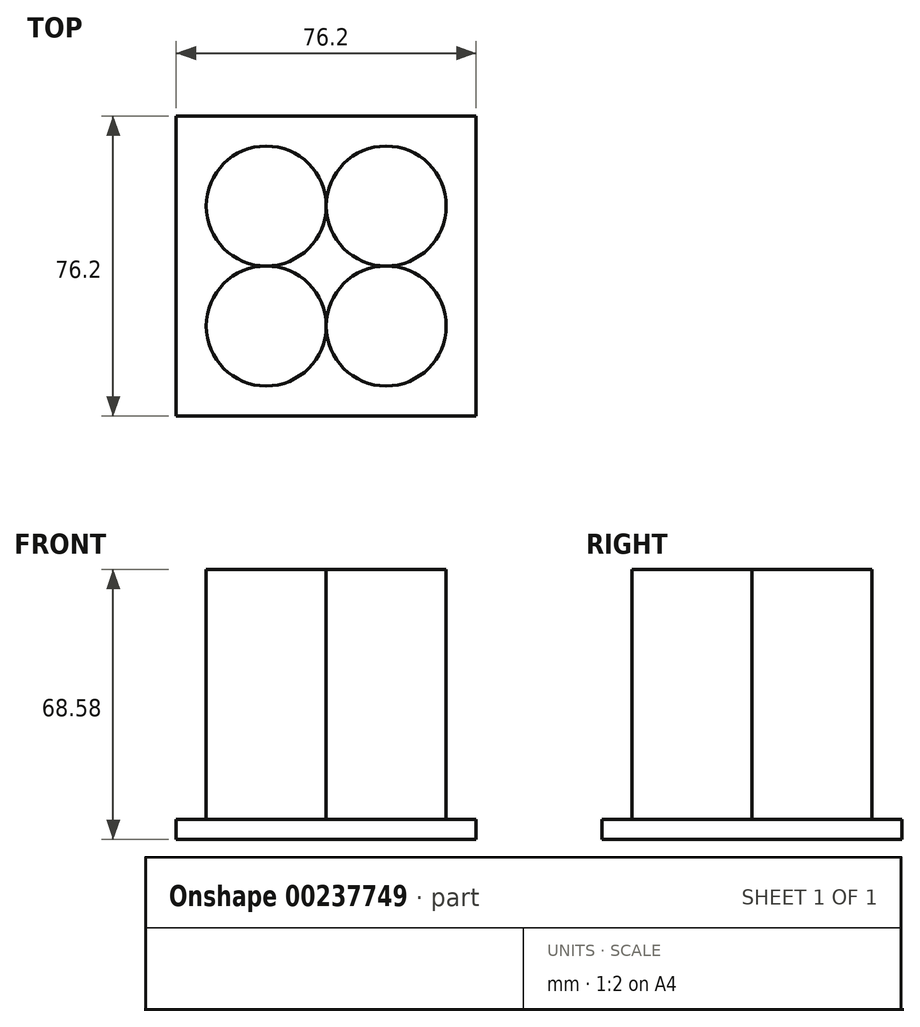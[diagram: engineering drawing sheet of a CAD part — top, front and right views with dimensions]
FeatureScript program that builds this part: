
annotation { "Feature Type Name" : "Feature", "Feature Type Description" : "" }
export const myFeature = defineFeature(function(context is Context, id is Id, definition is map)
    precondition{}
    {
        {
            var Q0;
            Q0=qCreatedBy(makeId("Top.planeOp"),FACE);
            var sketch = newSketch(context, id + "F0", { "sketchPlane" : qUnion([Q0])});
            skCircle(sketch, "E0", {"center": v(-15.24, -15.24) * mm, "radius": 15.24 * mm});
            skCircle(sketch, "E1", {"center": v(15.24, -15.24) * mm, "radius": 15.24 * mm});
            skCircle(sketch, "E2", {"center": v(-15.24, 15.24) * mm, "radius": 15.24 * mm});
            skCircle(sketch, "E3", {"center": v(15.24, 15.24) * mm, "radius": 15.24 * mm});
            skLineSegment(sketch, "E4", {"start": v(-15.24, 15.24) * mm, "end": v(-15.24, -15.24) * mm, "construction": true});
            skLineSegment(sketch, "E5", {"start": v(-15.24, 15.24) * mm, "end": v(15.24, 15.24) * mm, "construction": true});
            skLineSegment(sketch, "E6", {"start": v(15.24, -15.24) * mm, "end": v(-15.24, -15.24) * mm, "construction": true});
            skSolve(sketch);
        }
        {
            var Q0;
            {var subQ0=sQuery(id+"F0.wireOp",EDGE,"ICpDPUjX-ivMe-23Ei-ieje-qIsjfVPonkm3");var subQ1=makeQuery(id+"F0.imprint","INTERSECT",VERTEX,{"derivedFrom":[subQ0,sQuery(id+"F0.wireOp",EDGE,"1585de0c-b4fc-4455-9636-1ccd38715f07")]});Q0=makeQuery(id+"F0.imprint","IMPRINT",FACE,{"disambiguationData":[TD([[makeQuery(id+"F0.imprint","IMPRINT",EDGE,{"disambiguationData":[TD([[subQ1,-1.0]])],"derivedFrom":subQ0}),1.0]])]});}
            var Q1;
            {var subQ0=sQuery(id+"F0.wireOp",EDGE,"1585de0c-b4fc-4455-9636-1ccd38715f07");var subQ1=makeQuery(id+"F0.imprint","INTERSECT",VERTEX,{"derivedFrom":[sQuery(id+"F0.wireOp",EDGE,"ICpDPUjX-ivMe-23Ei-ieje-qIsjfVPonkm3"),subQ0]});Q1=makeQuery(id+"F0.imprint","IMPRINT",FACE,{"disambiguationData":[TD([[makeQuery(id+"F0.imprint","IMPRINT",EDGE,{"disambiguationData":[TD([[subQ1,1.0]])],"derivedFrom":subQ0}),1.0]])]});}
            var Q2;
            {var subQ0=sQuery(id+"F0.wireOp",EDGE,"8cf919d0-c88a-4376-973f-18324e1bfcb2");var subQ1=makeQuery(id+"F0.imprint","INTERSECT",VERTEX,{"derivedFrom":[sQuery(id+"F0.wireOp",EDGE,"1585de0c-b4fc-4455-9636-1ccd38715f07"),subQ0]});Q2=makeQuery(id+"F0.imprint","IMPRINT",FACE,{"disambiguationData":[TD([[makeQuery(id+"F0.imprint","IMPRINT",EDGE,{"disambiguationData":[TD([[subQ1,-1.0]])],"derivedFrom":subQ0}),1.0]])]});}
            var Q3;
            {var subQ0=sQuery(id+"F0.wireOp",EDGE,"0c448a11-c32a-4d7b-bc3d-f4b18554e8e6");var subQ1=makeQuery(id+"F0.imprint","INTERSECT",VERTEX,{"derivedFrom":[sQuery(id+"F0.wireOp",EDGE,"8cf919d0-c88a-4376-973f-18324e1bfcb2"),subQ0]});Q3=makeQuery(id+"F0.imprint","IMPRINT",FACE,{"disambiguationData":[TD([[makeQuery(id+"F0.imprint","IMPRINT",EDGE,{"disambiguationData":[TD([[subQ1,-1.0]])],"derivedFrom":subQ0}),1.0]])]});}
            var Q4;
            {var subQ0=sQuery(id+"F0.wireOp",EDGE,"877ee094-fdc9-495d-ab0e-c5a52c05f9cd");var subQ4=makeQuery(id+"F0.imprint","INTERSECT",VERTEX,{"derivedFrom":[sQuery(id+"F0.wireOp",EDGE,"8cf919d0-c88a-4376-973f-18324e1bfcb2"),subQ0]});Q4=makeQuery(id+"F0.imprint","IMPRINT",FACE,{"disambiguationData":[TD([[makeQuery(id+"F0.imprint","IMPRINT",EDGE,{"disambiguationData":[TD([[subQ4,1.0]])],"derivedFrom":subQ0}),1.0]])]});}
            var Q5;
            {var subQ0=sQuery(id+"F0.wireOp",EDGE,"d8245553-00ec-417b-91d8-0db8256ae251");var subQ4=makeQuery(id+"F0.imprint","INTERSECT",VERTEX,{"derivedFrom":[sQuery(id+"F0.wireOp",EDGE,"1585de0c-b4fc-4455-9636-1ccd38715f07"),subQ0]});Q5=makeQuery(id+"F0.imprint","IMPRINT",FACE,{"disambiguationData":[TD([[makeQuery(id+"F0.imprint","IMPRINT",EDGE,{"disambiguationData":[TD([[subQ4,1.0]])],"derivedFrom":subQ0}),1.0]])]});}
            var Q6;
            {var subQ0=sQuery(id+"F0.wireOp",EDGE,"E0");var subQ1=makeQuery(id+"F0.imprint","INTERSECT",VERTEX,{"derivedFrom":[sQuery(id+"F0.wireOp",EDGE,"d8245553-00ec-417b-91d8-0db8256ae251"),subQ0]});Q6=makeQuery(id+"F0.imprint","IMPRINT",FACE,{"disambiguationData":[TD([[makeQuery(id+"F0.imprint","IMPRINT",EDGE,{"disambiguationData":[TD([[subQ1,1.0]])],"derivedFrom":subQ0}),1.0]])]});}
            var Q7;
            {var subQ0=sQuery(id+"F0.wireOp",EDGE,"E1");var subQ1=makeQuery(id+"F0.imprint","INTERSECT",VERTEX,{"derivedFrom":[subQ0,sQuery(id+"F0.wireOp",EDGE,"339a6f02-9774-4792-871e-ff289bf21d4b")]});Q7=makeQuery(id+"F0.imprint","IMPRINT",FACE,{"disambiguationData":[TD([[makeQuery(id+"F0.imprint","IMPRINT",EDGE,{"disambiguationData":[TD([[subQ1,-1.0]])],"derivedFrom":subQ0}),1.0]])]});}
            var Q8;
            {var subQ0=sQuery(id+"F0.wireOp",EDGE,"339a6f02-9774-4792-871e-ff289bf21d4b");var subQ1=makeQuery(id+"F0.imprint","INTERSECT",VERTEX,{"derivedFrom":[sQuery(id+"F0.wireOp",EDGE,"0c448a11-c32a-4d7b-bc3d-f4b18554e8e6"),subQ0]});Q8=makeQuery(id+"F0.imprint","IMPRINT",FACE,{"disambiguationData":[TD([[makeQuery(id+"F0.imprint","IMPRINT",EDGE,{"disambiguationData":[TD([[subQ1,-1.0]])],"derivedFrom":subQ0}),1.0]])]});}
            var Q9;
            {var subQ0=sQuery(id+"F0.wireOp",EDGE,"E2");var subQ1=makeQuery(id+"F0.imprint","INTERSECT",VERTEX,{"derivedFrom":[sQuery(id+"F0.wireOp",EDGE,"E0"),subQ0]});Q9=makeQuery(id+"F0.imprint","IMPRINT",FACE,{"disambiguationData":[TD([[makeQuery(id+"F0.imprint","IMPRINT",EDGE,{"disambiguationData":[TD([[subQ1,1.0]])],"derivedFrom":subQ0}),1.0]])]});}
            var Q10;
            {var subQ0=sQuery(id+"F0.wireOp",EDGE,"E3");var subQ1=makeQuery(id+"F0.imprint","INTERSECT",VERTEX,{"derivedFrom":[sQuery(id+"F0.wireOp",EDGE,"E2"),subQ0]});Q10=makeQuery(id+"F0.imprint","IMPRINT",FACE,{"disambiguationData":[TD([[makeQuery(id+"F0.imprint","IMPRINT",EDGE,{"disambiguationData":[TD([[subQ1,1.0]])],"derivedFrom":subQ0}),1.0]])]});}
            var Q11;
            {var subQ0=sQuery(id+"F0.wireOp",EDGE,"e1cb0e98-296c-46c9-8ced-bc2852320654");var subQ1=makeQuery(id+"F0.imprint","INTERSECT",VERTEX,{"derivedFrom":[sQuery(id+"F0.wireOp",EDGE,"339a6f02-9774-4792-871e-ff289bf21d4b"),subQ0]});Q11=makeQuery(id+"F0.imprint","IMPRINT",FACE,{"disambiguationData":[TD([[makeQuery(id+"F0.imprint","IMPRINT",EDGE,{"disambiguationData":[TD([[subQ1,1.0]])],"derivedFrom":subQ0}),1.0]])]});}
            var Q12;
            Q12=sQuery(id+"F0.wireOp",EDGE,"877ee094-fdc9-495d-ab0e-c5a52c05f9cd");
            var Q13;
            Q13=sQuery(id+"F0.wireOp",EDGE,"ICpDPUjX-ivMe-23Ei-ieje-qIsjfVPonkm3");
            var Q14;
            Q14=sQuery(id+"F0.wireOp",EDGE,"339a6f02-9774-4792-871e-ff289bf21d4b");
            var Q15;
            Q15=sQuery(id+"F0.wireOp",EDGE,"E1");
            var Q16;
            Q16=sQuery(id+"F0.wireOp",EDGE,"E0");
            var Q17;
            Q17=sQuery(id+"F0.wireOp",EDGE,"0c448a11-c32a-4d7b-bc3d-f4b18554e8e6");
            var Q18;
            Q18=sQuery(id+"F0.wireOp",EDGE,"d8245553-00ec-417b-91d8-0db8256ae251");
            var Q19;
            Q19=sQuery(id+"F0.wireOp",EDGE,"8cf919d0-c88a-4376-973f-18324e1bfcb2");
            var Q20;
            Q20=sQuery(id+"F0.wireOp",EDGE,"1585de0c-b4fc-4455-9636-1ccd38715f07");
            extrude(context, id + "F1", {"entities" : qUnion([Q0, Q1, Q2, Q3, Q4, Q5, Q6, Q7, Q8, Q9, Q10, Q11]), "surfaceEntities" : qUnion([Q12, Q13, Q14, Q15, Q16, Q17, Q18, Q19, Q20]), "depth" : 63.5 * mm});
        }
        {
            var Q0;
            Q0=qCreatedBy(makeId("Front.planeOp"),FACE);
            var sketch = newSketch(context, id + "F2", { "sketchPlane" : qUnion([Q0])});
            skLineSegment(sketch, "E7.bottom", {"start": v(38.1, 0) * mm, "end": v(-38.1, 0) * mm});
            skLineSegment(sketch, "E7.top", {"start": v(38.1, -5.08) * mm, "end": v(-38.1, -5.08) * mm});
            skLineSegment(sketch, "E7.left", {"start": v(38.1, 0) * mm, "end": v(38.1, -5.08) * mm});
            skLineSegment(sketch, "E7.right", {"start": v(-38.1, 0) * mm, "end": v(-38.1, -5.08) * mm});
            skSolve(sketch);
        }
        {
            var Q0;
            Q0=makeQuery(id+"F2.imprint","IMPRINT",FACE,{"disambiguationData":[TD([[makeQuery(id+"F2.imprint","IMPRINT",EDGE,{"derivedFrom":sQuery(id+"F2.wireOp",EDGE,"E7.bottom")}),1.0]])]});
            var Q1;
            Q1=makeQuery(id+"F2.imprint","IMPRINT",FACE,{"disambiguationData":[TD([[makeQuery(id+"F2.imprint","IMPRINT",EDGE,{"derivedFrom":sQuery(id+"F2.wireOp",EDGE,"b8d46107-f48f-4c03-8077-e383a4ff9cb9.bottom")}),1.0]])]});
            var Q2;
            Q2=sQuery(id+"F2.wireOp",EDGE,"E7.bottom");
            extrude(context, id + "F3", {"entities" : qUnion([Q0, Q1]), "surfaceEntities" : qUnion([Q2]), "endBound" : BoundingType.SYMMETRIC, "oppositeDirection" : true, "depth" : 76.2 * mm});
        }
    });
